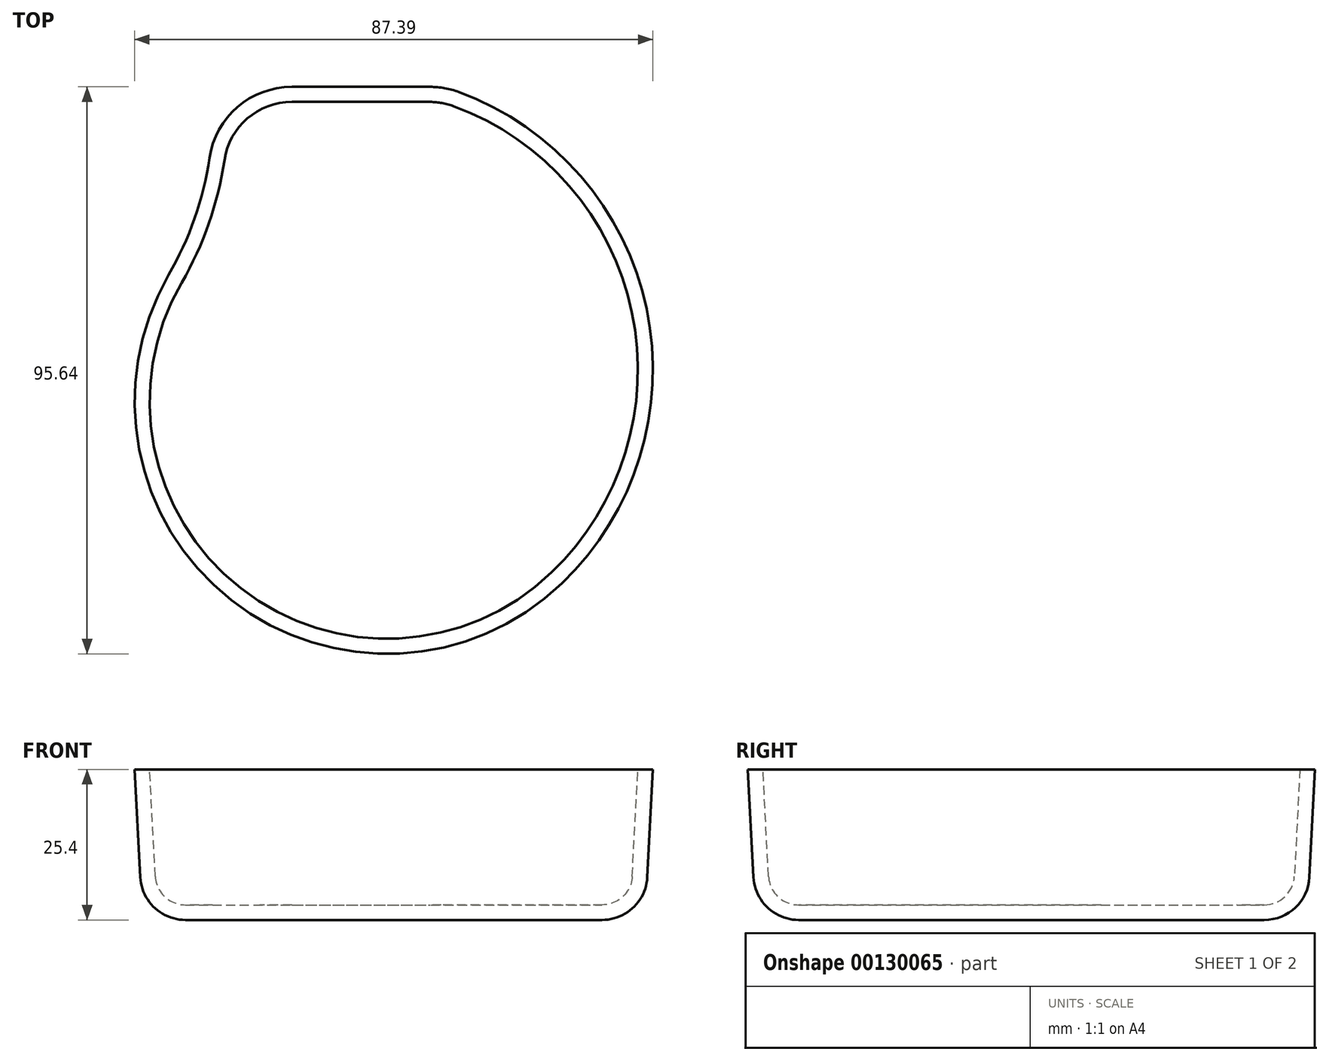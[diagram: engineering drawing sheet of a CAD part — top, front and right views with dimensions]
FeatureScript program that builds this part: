
annotation { "Feature Type Name" : "Feature", "Feature Type Description" : "" }
export const myFeature = defineFeature(function(context is Context, id is Id, definition is map)
    precondition{}
    {
        {
            var Q0;
            Q0=qCreatedBy(makeId("Top.planeOp"),FACE);
            var sketch = newSketch(context, id + "F0", { "sketchPlane" : qUnion([Q0])});
            skArc(sketch, "E0", {"start": v(-35.69, 20.66) * mm, "mid": v(-25.43, -32.45) * mm, "end": v(28.59, -29.71) * mm});
            skLineSegment(sketch, "E1", {"start": v(-16.05, 51.75) * mm, "end": v(7.27, 51.75) * mm});
            skArc(sketch, "E2", {"start": v(-35.69, 20.66) * mm, "mid": v(-31.2, 30.45) * mm, "end": v(-28.61, 40.9) * mm});
            skArc(sketch, "E3", {"start": v(28.59, -29.71) * mm, "mid": v(42.46, 15.32) * mm, "end": v(11.65, 50.97) * mm});
            skPoint(sketch, "E4.visualSharp", {"position": v(-28.05, 51.75) * mm});
            skArc(sketch, "E4.filletArc", {"start": v(-16.05, 51.75) * mm, "mid": v(-24.35, 48.66) * mm, "end": v(-28.61, 40.9) * mm});
            skPoint(sketch, "E5.visualSharp", {"position": v(9.35, 51.75) * mm});
            skArc(sketch, "E5.filletArc", {"start": v(11.65, 50.97) * mm, "mid": v(9.5, 51.55) * mm, "end": v(7.27, 51.75) * mm});
            skSolve(sketch);
        }
        {
            var Q0;
            Q0=makeQuery(id+"F0.imprint","IMPRINT",FACE,{"disambiguationData":[TD([[makeQuery(id+"F0.imprint","IMPRINT",EDGE,{"derivedFrom":sQuery(id+"F0.wireOp",EDGE,"E0")}),1.0]])]});
            extrude(context, id + "F1", {"entities" : qUnion([Q0]), "depth" : 25.4 * mm, "hasDraft" : true, "draftAngle" : 3 * degree});
        }
        {
            var Q0;
            Q0=makeQuery(id+"F1.opExtrude","CAP_EDGE",EDGE,{"disambiguationData":[OSD([sQuery(id+"F0.wireOp",EDGE,"E3")])],"isStart":true});
            fillet(context, id + "F2", {"entities" : qUnion([Q0]), "radius" : 7.62 * mm, "tangentPropagation" : true, "allowEdgeOverflow" : false});
        }
        {
            var Q0;
            Q0=makeQuery(id+"F1.opExtrude","CAP_FACE",FACE,{"disambiguationData":[OSD([sQuery(id+"F0.wireOp",EDGE,"E0"),sQuery(id+"F0.wireOp",EDGE,"E1"),sQuery(id+"F0.wireOp",EDGE,"E2"),sQuery(id+"F0.wireOp",EDGE,"E3"),sQuery(id+"F0.wireOp",EDGE,"E4.filletArc"),sQuery(id+"F0.wireOp",EDGE,"E5.filletArc")])],"isStart":false});
            shell(context, id + "F3", {"entities" : qUnion([Q0]), "thickness" : 2.54 * mm});
        }
    });
